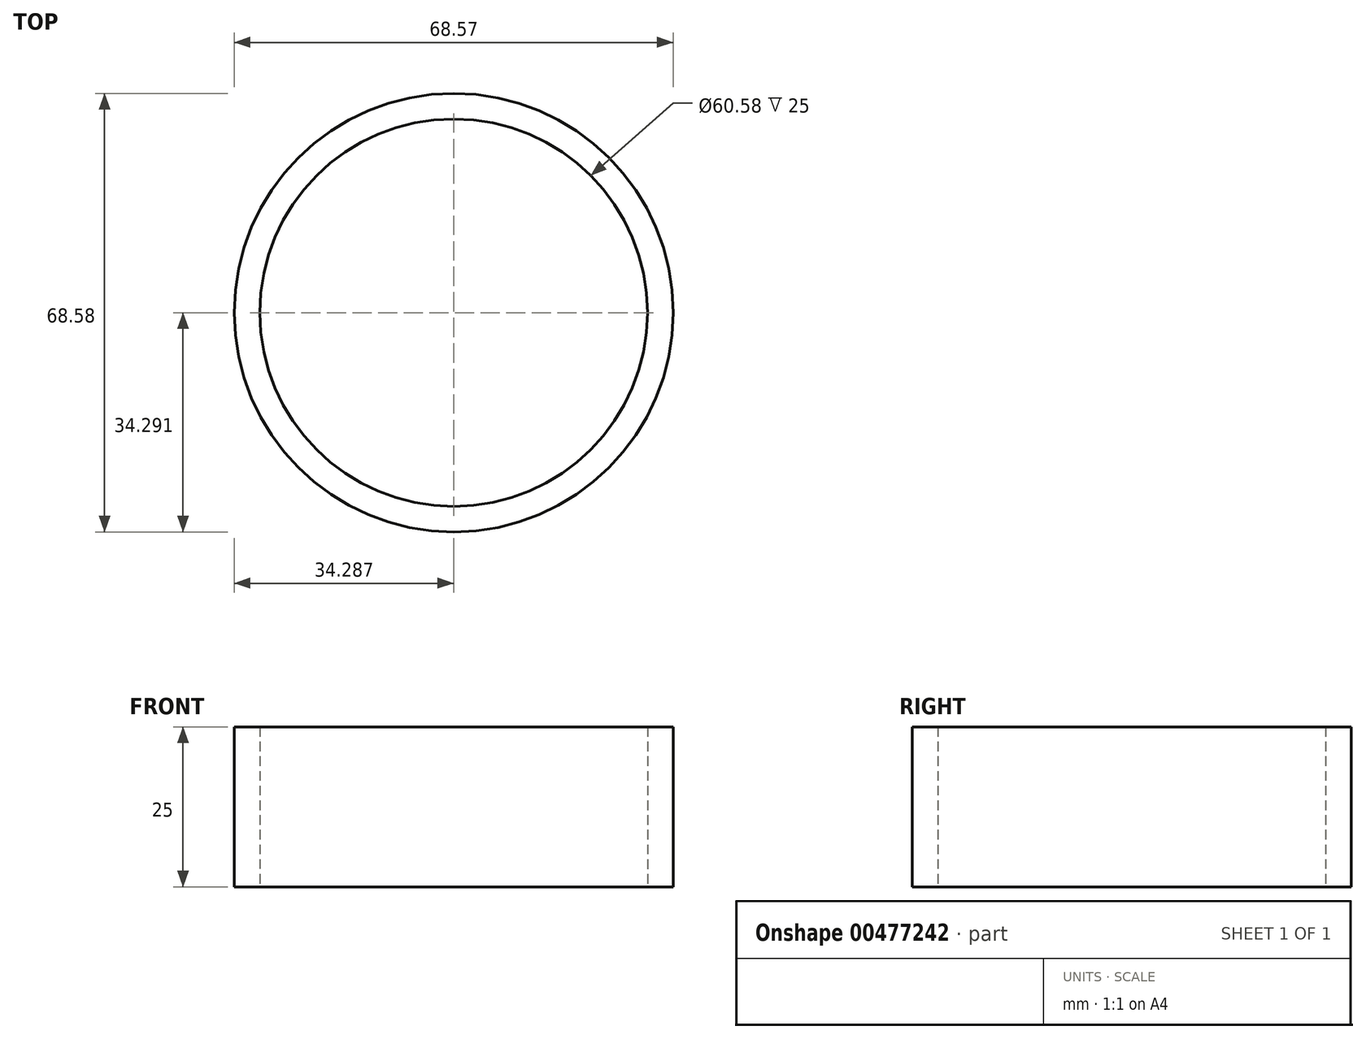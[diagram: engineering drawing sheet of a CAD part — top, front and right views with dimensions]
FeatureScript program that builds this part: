
annotation { "Feature Type Name" : "Feature", "Feature Type Description" : "" }
export const myFeature = defineFeature(function(context is Context, id is Id, definition is map)
    precondition{}
    {
        {
            var Q0;
            Q0=qCreatedBy(makeId("Top.planeOp"),FACE);
            var sketch = newSketch(context, id + "F0", { "sketchPlane" : qUnion([Q0])});
            skCircle(sketch, "E0", {"center": v(0.69, -0.23) * mm, "radius": 34.29 * mm});
            skCircle(sketch, "E1", {"center": v(0.69, -0.23) * mm, "radius": 30.29 * mm});
            skSolve(sketch);
        }
        {
            var Q0;
            Q0=makeQuery(id+"F0.imprint","IMPRINT",FACE,{"disambiguationData":[TD([[makeQuery(id+"F0.imprint","IMPRINT",EDGE,{"derivedFrom":sQuery(id+"F0.wireOp",EDGE,"E0")}),1.0]])]});
            extrude(context, id + "F1", {"entities" : qUnion([Q0]), "depth" : 25 * mm});
        }
    });
